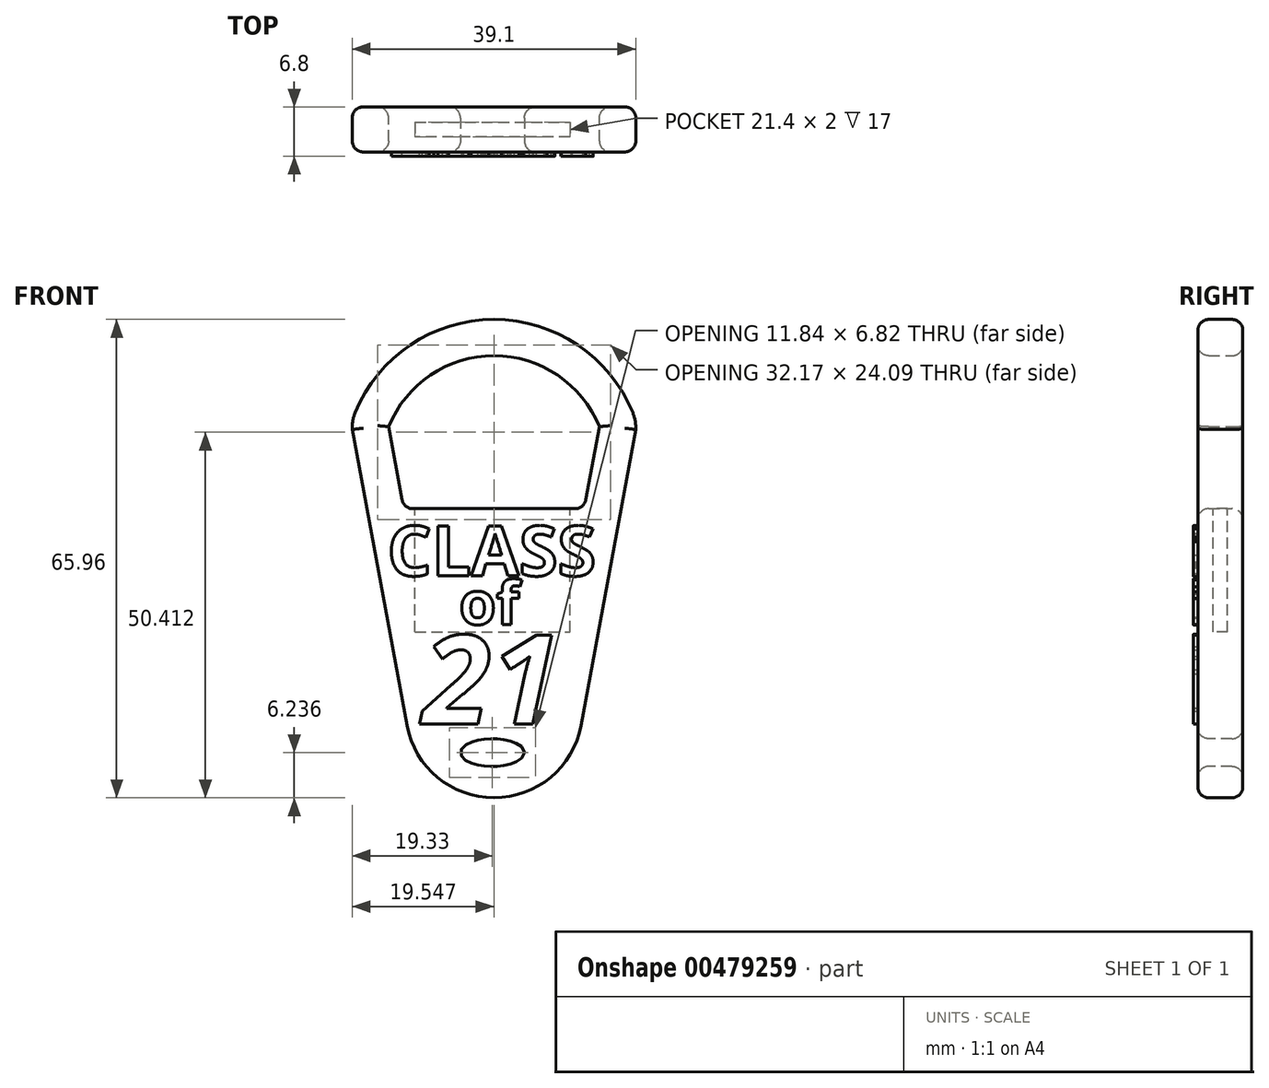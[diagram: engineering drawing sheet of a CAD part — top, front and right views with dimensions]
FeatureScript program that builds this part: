
annotation { "Feature Type Name" : "Feature", "Feature Type Description" : "" }
export const myFeature = defineFeature(function(context is Context, id is Id, definition is map)
    precondition{}
    {
        {
            var Q0;
            Q0=qCreatedBy(makeId("Front.planeOp"),FACE);
            var sketch = newSketch(context, id + "F0", { "sketchPlane" : qUnion([Q0])});
            skLineSegment(sketch, "E0", {"start": v(0.22, 53.5) * mm, "end": v(0.22, -27.22) * mm, "construction": true});
            skLineSegment(sketch, "E1", {"start": v(19.76, 12.33) * mm, "end": v(12.22, -28.48) * mm});
            skLineSegment(sketch, "E2.MirrorCS", {"start": v(-19.33, 12.33) * mm, "end": v(-11.78, -28.48) * mm});
            skLineSegment(sketch, "E3.0", {"start": v(-14.31, 12.71) * mm, "end": v(-12.22, 1.4) * mm});
            skLineSegment(sketch, "E3.3", {"start": v(14.75, 12.71) * mm, "end": v(12.66, 1.4) * mm});
            skLineSegment(sketch, "E4", {"start": v(-12.22, 1.4) * mm, "end": v(12.66, 1.4) * mm});
            skPoint(sketch, "E5", {"position": v(0.22, 20.6) * mm});
            skPoint(sketch, "E6", {"position": v(-14.31, 12.71) * mm});
            skPoint(sketch, "E7.MirrorP", {"position": v(14.75, 12.71) * mm});
            skArc(sketch, "E8", {"start": v(14.75, 12.71) * mm, "mid": v(0.22, 22.5) * mm, "end": v(-14.31, 12.71) * mm});
            skArc(sketch, "E9.0", {"start": v(19.62, 13.97) * mm, "mid": v(0.56, 27.5) * mm, "end": v(-18.94, 14.6) * mm});
            skArc(sketch, "E10", {"start": v(-18.94, 14.6) * mm, "mid": v(-19.26, 13.5) * mm, "end": v(-19.33, 12.33) * mm});
            skArc(sketch, "E11.MirrorCS", {"start": v(19.38, 14.6) * mm, "mid": v(19.7, 13.5) * mm, "end": v(19.76, 12.33) * mm});
            skPoint(sketch, "E12.orphan", {"position": v(-21.9, 26.19) * mm});
            skPoint(sketch, "E13.orphan", {"position": v(22.32, 26.19) * mm});
            skPoint(sketch, "E14.MirrorCS.start.orphan", {"position": v(0.22, 25.6) * mm});
            skArc(sketch, "E15", {"start": v(-11.78, -28.48) * mm, "mid": v(0.22, -38.46) * mm, "end": v(12.22, -28.48) * mm});
            skPoint(sketch, "E16.MirrorCS.end.orphan", {"position": v(0.22, -28.48) * mm});
            skPoint(sketch, "E16.MirrorCS.start.orphan", {"position": v(-11.78, -28.48) * mm});
            skLineSegment(sketch, "E17", {"start": v(-11.78, -28.48) * mm, "end": v(12.22, -28.48) * mm, "construction": true});
            skSolve(sketch);
        }
        {
            var Q0;
            Q0=qSketchRegion(id+"F0",true);
            extrude(context, id + "F1", {"entities" : qUnion([Q0]), "depth" : 6.2 * mm});
        }
        {
            var Q0;
            Q0=makeQuery(id+"F1.opExtrude","CAP_FACE",FACE,{"disambiguationData":[OSD([sQuery(id+"F0.wireOp",EDGE,"E1"),sQuery(id+"F0.wireOp",EDGE,"E2.MirrorCS"),sQuery(id+"F0.wireOp",EDGE,"E3.0"),sQuery(id+"F0.wireOp",EDGE,"E3.3"),sQuery(id+"F0.wireOp",EDGE,"E4"),sQuery(id+"F0.wireOp",EDGE,"E8"),sQuery(id+"F0.wireOp",EDGE,"E9.0"),sQuery(id+"F0.wireOp",EDGE,"E10"),sQuery(id+"F0.wireOp",EDGE,"E11.MirrorCS"),sQuery(id+"F0.wireOp",EDGE,"E15")])],"isStart":false});
            var sketch = newSketch(context, id + "F2", { "sketchPlane" : qUnion([Q0])});
            skEllipse(sketch, "E18", {"center": v(0, -32.22) * mm, "majorRadius": 4.42 * mm, "minorRadius": 1.9 * mm, "majorAxis": v(1, 0)});
            skSolve(sketch);
        }
        {
            var Q0;
            Q0=makeQuery(id+"F2.imprint","IMPRINT",FACE,{"disambiguationData":[TD([[makeQuery(id+"F2.imprint","IMPRINT",EDGE,{"derivedFrom":sQuery(id+"F2.wireOp",EDGE,"E18")}),1.0]])]});
            extrude(context, id + "F3", {"entities" : qUnion([Q0]), "operationType" : NewBodyOperationType.REMOVE, "oppositeDirection" : true, "depth" : 6.5 * mm});
        }
        {
            var Q0;
            Q0=makeQuery(id+"F1.opExtrude","SWEPT_FACE",FACE,{"disambiguationData":[OSD([sQuery(id+"F0.wireOp",EDGE,"E4")])]});
            var sketch = newSketch(context, id + "F4", { "sketchPlane" : qUnion([Q0])});
            skLineSegment(sketch, "E19", {"start": v(0, -2.1) * mm, "end": v(10.7, -2.1) * mm});
            skLineSegment(sketch, "E20.0", {"start": v(0, -4.1) * mm, "end": v(10.7, -4.1) * mm});
            skLineSegment(sketch, "E21", {"start": v(10.7, -2.1) * mm, "end": v(10.7, -4.1) * mm});
            skLineSegment(sketch, "E22", {"start": v(0, -2.1) * mm, "end": v(0, -4.1) * mm, "construction": true});
            skLineSegment(sketch, "E23.MirrorCS", {"start": v(0, -2.1) * mm, "end": v(-10.7, -2.1) * mm});
            skLineSegment(sketch, "E24.MirrorCS", {"start": v(-10.7, -2.1) * mm, "end": v(-10.7, -4.1) * mm});
            skLineSegment(sketch, "E25.MirrorCS", {"start": v(0, -4.1) * mm, "end": v(-10.7, -4.1) * mm});
            skSolve(sketch);
        }
        {
            var Q0;
            Q0=makeQuery(id+"F4.imprint","IMPRINT",FACE,{"disambiguationData":[TD([[makeQuery(id+"F4.imprint","IMPRINT",EDGE,{"derivedFrom":sQuery(id+"F4.wireOp",EDGE,"E19")}),-1.0]])]});
            extrude(context, id + "F5", {"entities" : qUnion([Q0]), "operationType" : NewBodyOperationType.REMOVE, "oppositeDirection" : true, "depth" : 17 * mm});
        }
        {
            var Q0;
            Q0=makeQuery(id+"F1.opExtrude","SWEPT_EDGE",EDGE,{"disambiguationData":[OSD([sQuery(id+"F0.wireOp",EDGE,"E3.0"),sQuery(id+"F0.wireOp",EDGE,"E4")])]});
            var Q1;
            Q1=makeQuery(id+"F1.opExtrude","SWEPT_EDGE",EDGE,{"disambiguationData":[OSD([sQuery(id+"F0.wireOp",EDGE,"E3.3"),sQuery(id+"F0.wireOp",EDGE,"E4")])]});
            var Q2;
            Q2=makeQuery(id+"F1.opExtrude","CAP_FACE",FACE,{"disambiguationData":[OSD([sQuery(id+"F0.wireOp",EDGE,"E1"),sQuery(id+"F0.wireOp",EDGE,"E2.MirrorCS"),sQuery(id+"F0.wireOp",EDGE,"E3.0"),sQuery(id+"F0.wireOp",EDGE,"E3.3"),sQuery(id+"F0.wireOp",EDGE,"E4"),sQuery(id+"F0.wireOp",EDGE,"E8"),sQuery(id+"F0.wireOp",EDGE,"E9.0"),sQuery(id+"F0.wireOp",EDGE,"E10"),sQuery(id+"F0.wireOp",EDGE,"E11.MirrorCS"),sQuery(id+"F0.wireOp",EDGE,"E15")])],"isStart":false});
            var Q3;
            Q3=makeQuery(id+"F1.opExtrude","CAP_FACE",FACE,{"disambiguationData":[OSD([sQuery(id+"F0.wireOp",EDGE,"E1"),sQuery(id+"F0.wireOp",EDGE,"E2.MirrorCS"),sQuery(id+"F0.wireOp",EDGE,"E3.0"),sQuery(id+"F0.wireOp",EDGE,"E3.3"),sQuery(id+"F0.wireOp",EDGE,"E4"),sQuery(id+"F0.wireOp",EDGE,"E8"),sQuery(id+"F0.wireOp",EDGE,"E9.0"),sQuery(id+"F0.wireOp",EDGE,"E10"),sQuery(id+"F0.wireOp",EDGE,"E11.MirrorCS"),sQuery(id+"F0.wireOp",EDGE,"E15")])],"isStart":true});
            fillet(context, id + "F6", {"entities" : qUnion([Q0, Q1, Q2, Q3]), "radius" : 1.5 * mm, "tangentPropagation" : true, "allowEdgeOverflow" : false});
        }
        {
            var Q0;
            Q0=makeQuery(id+"F1.opExtrude","CAP_FACE",FACE,{"disambiguationData":[OSD([sQuery(id+"F0.wireOp",EDGE,"E1"),sQuery(id+"F0.wireOp",EDGE,"E2.MirrorCS"),sQuery(id+"F0.wireOp",EDGE,"E3.0"),sQuery(id+"F0.wireOp",EDGE,"E3.3"),sQuery(id+"F0.wireOp",EDGE,"E4"),sQuery(id+"F0.wireOp",EDGE,"E8"),sQuery(id+"F0.wireOp",EDGE,"E9.0"),sQuery(id+"F0.wireOp",EDGE,"E10"),sQuery(id+"F0.wireOp",EDGE,"E11.MirrorCS"),sQuery(id+"F0.wireOp",EDGE,"E15")])],"isStart":false});
            var sketch = newSketch(context, id + "F7", { "sketchPlane" : qUnion([Q0])});
            skText(sketch, "E26", { "text": "CLASS", "fontName": "NotoSans-Bold.ttf"});
            skText(sketch, "E27", { "text": "of", "fontName": "NotoSans-Bold.ttf"});
            skText(sketch, "E28", { "text": "21", "fontName": "NotoSans-BoldItalic.ttf"});
            const initialGuessF7  = {"E26": [-0.0145, -0.00785, 1, 0, 0.00692], "E27": [-0.0046, -0.01456, 1, 0, 0.00594], "E28": [-0.00965, -0.0283, 1, 0, 0.01234]};
            skSetInitialGuess(sketch, initialGuessF7);
            skSolve(sketch);
        }
        {
            var Q0;
            Q0 = qSketchRegion(id + "F7", true);
            extrude(context, id + "F8", {"entities" : qUnion([Q0]), "operationType" : NewBodyOperationType.ADD, "depth" : .6 * mm, "offsetDistance" : 25 * mm});
        }
    });
